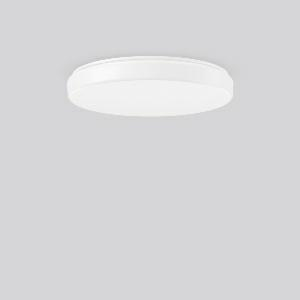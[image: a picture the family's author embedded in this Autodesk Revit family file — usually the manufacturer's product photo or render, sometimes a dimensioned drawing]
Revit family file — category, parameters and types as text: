
# Revit family: flat_polymero_kreis_slim_312240_002_1_15d9
name_source: partatom
category: Lighting Fixtures
units: mm (PartAtom-declared; Revit-internal decimal feet)

## family parameters
Cut with Voids When Loaded = No
Host = Face
Light Source = No
Part Type = Normal
Room Calculation Point = No
Round Connector Dimension = Use Diameter
Shared = No

## types (1)
- FLAT POLYMERO KREIS SLIM (1 x LED Modul 830, 2600 lm, 3000)
    Apparent Load = 24 VA
    CIE Flux Codes = 41 72 91 83 100
    Color Rendering = 80
    Color Temperature = 3000
    Default Elevation = 1800 mm
    Description = Series: FLAT POLYMERO KREIS SLIM
Flat decorative round LED surface-mounted luminaire. Base: metal, powder-coated. Diffuser made of non-yellowing plastic (PMMA), opal. Diffuser fastening: patented push system. Suitable for Ceiling mounting, Wall (surface). 
Colour: white
Diameter: 460 mm
Height: 70 mm
Lamp: LED exchangeable
Socket: without socket
Colour temperature: 3000K
Colour rendering index (CRI): 83
System power: 24 W
Rated luminous flux: 2600 lm
Luminous efficiency: 108 lm/W
Control gear: AC Strom, dim.Ph.an-/abschnitt
Protection class: I
Type of protection: IP 40
    Height = 70 mm
    Lamp = 1 x LED Modul 830
    Lamp Light Flux = 2600 lm
    Lamp count = 1
    Length = 460 mm
    Lifetime = 50000 h
    Luminous efficacy = 108 lm/W
    Manufacturer = RZB
    ModVariant = No
    Model = 312240.002.1
    Mounting Place = Ceiling, Wall
    Mounting Type = Surface mounted
    Number of Poles = 1
    OnlyDefault = Yes
    Power Factor = 1
    Product Name = FLAT POLYMERO KREIS SLIM
    Product group = Surface mounted ceiling and wall luminaires
    ProductGroupID = 305
    Protection Class = Protection class I
    Protection Degree = IP 40
    RLX_Detail_Level = 1
    RLX_Emergency_Light_Flux = 0 lm
    RLX_Emergency_Type = 0
    RLX_Emergency_Type_DB = No
    RlxData = <blob elided: 57705 chars, md5=4a1f738c>
    Socket = socket
    Standby Power = 0 W
    System Light Flux = 2600 lm
    System Power = 24 W
    Type Comments = Product without accessories
    Type Image = 312086.002.jpg
    URL = http://relux.com
    VarID = ---
    Voltage = 230 V
    Voltage Range = 220-240 V
    Weight = 0.00 kg
    Width = 0 mm  [stored 0 ft]

note: [stored X ft] marks values corroborated as IEEE doubles in the binary element streams (Revit-internal decimal feet)

## geometry (parser evidence)
native form markers: Blend x4, Sweep x13
no freeform markers — native parametric forms only
